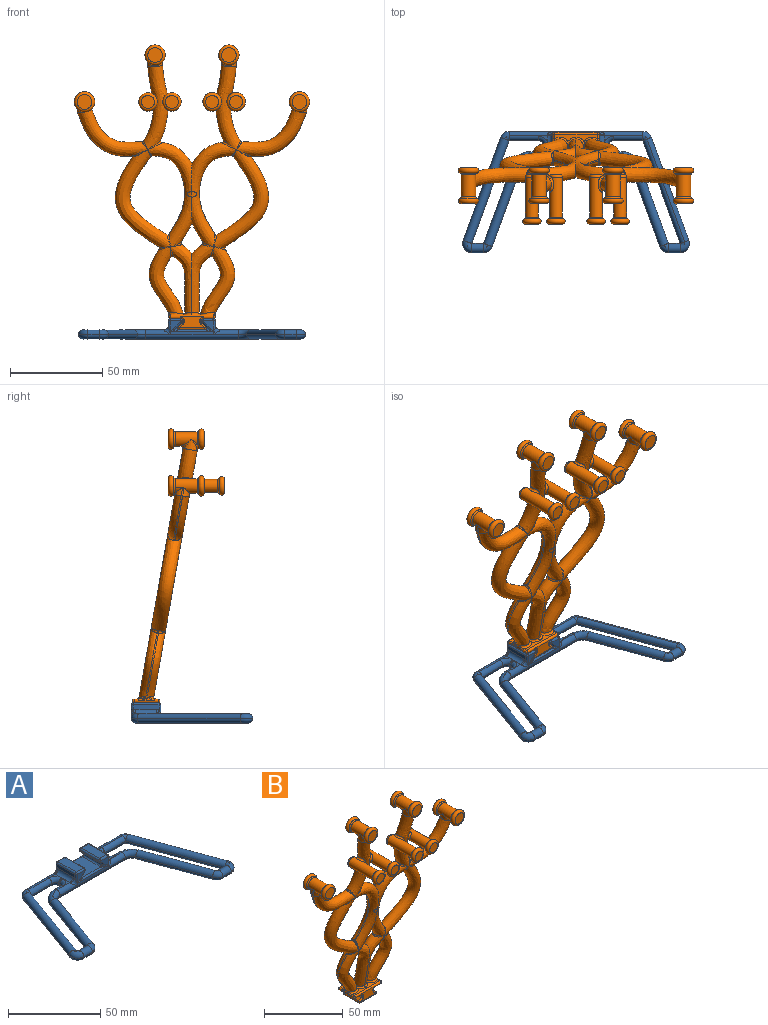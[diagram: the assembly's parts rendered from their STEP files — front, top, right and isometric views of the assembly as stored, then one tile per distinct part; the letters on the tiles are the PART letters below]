
ASSEMBLY  parts=2 mates=1
PART A: 190 faces, bbox 123.8x66.6x10.9 mm
  f0: cylinder r=1mm len=13.55mm, axis (0,1,0), area 31.9mm2, adj f1,f2,f27,f28
  f1: bspline ~1.81x1.19mm, area 1.3mm2, adj f0,f27,f28,f75,f76,f92
  f2: bspline ~1.81x1.19mm, area 1.3mm2, adj f0,f27,f28,f86,f88,f93
  f3: plane 118.01x60.78mm, normal (0,0,-1), area 357mm2, adj f40,f41,f42,f43,f44,f45,f46,f47
  f4: plane 50x7.4mm, normal (0,-1,0), area 70.3mm2, adj f12,f39,f66,f83,f86,f87,f88,f91
  f5: plane 72.41x7.4mm, normal (0,1,0), area 70.3mm2, adj f6,f31,f74,f75,f76,f78,f80,f81
  f6: cylinder r=5mm len=4.7mm, axis (0,0,-1), area 0mm2, adj f5,f7,f32,f73
  f7: plane 55.78x20.3mm, normal (-0.94,0.34,0), area 0mm2, adj f6,f8,f33,f72
  f8: cylinder r=5mm len=6.71mm, axis (0,0,-1), area 0mm2, adj f7,f9,f34,f71
  f9: plane 6.39x0mm, normal (0,-1,0), area 0mm2, adj f8,f10,f35,f70
  f10: cylinder r=5mm len=4.7mm, axis (0,0,-1), area 0mm2, adj f9,f11,f36,f69
  f11: plane 43.2x15.72mm, normal (0.94,-0.34,0), area 0mm2, adj f10,f12,f37,f68
  f12: cylinder r=5mm len=4.7mm, axis (0,0,-1), area 0mm2, adj f4,f11,f38,f67
  f13: plane 60.78x43.76mm, normal (0,0,1), area 10.7mm2, adj f31,f32,f33,f34,f35,f36,f37,f38
  f14: plane 4.75x0mm, normal (0,1,0), area 0mm2, adj f23,f49,f55,f60
  f15: plane 1x0mm, normal (-1,0,0), area 0mm2, adj f50,f51,f55,f56
  f16: plane 15.95x0mm, normal (0,-1,0), area 0mm2, adj f17,f46,f51,f54
  f17: cylinder r=0mm len=0mm, axis (0,0,-1), area 0mm2, adj f16,f18,f44,f57
  f18: plane 55.78x20.3mm, normal (0.94,-0.34,0), area 0mm2, adj f17,f19,f42,f59
  f19: cylinder r=0mm len=0mm, axis (0,0,-1), area 0mm2, adj f18,f20,f40,f61
  f20: plane 6.39x0mm, normal (0,1,0), area 0mm2, adj f19,f21,f41,f63
  f21: cylinder r=0mm len=0mm, axis (0,0,-1), area 0mm2, adj f20,f22,f43,f65
  f22: plane 43.2x15.72mm, normal (-0.94,0.34,0), area 0mm2, adj f21,f23,f45,f64
  f23: cylinder r=10mm len=9.4mm, axis (0,0,-1), area 0mm2, adj f14,f22,f47,f62
  f24: plane 14x2.63mm, normal (-1,0,0), area 33.8mm2, adj f80,f83,f84,f95,f96,f97
  f25: plane 14x0.49mm, normal (1,0,0), area 6.8mm2, adj f29,f30,f78,f91
  f26: plane 14x5.45mm, normal (0,0,1), area 76.3mm2, adj f29,f81,f84,f87
  f27: plane 14.01x13.79mm, normal (0,0,1), area 192.8mm2, adj f0,f1,f2,f75,f86,f99,f100,f101
  f28: plane 14.01x2.01mm, normal (0.71,0,-0.71), area 39.6mm2, adj f0,f1,f2,f30,f76,f88
  f29: cylinder r=1mm len=14mm, axis (0,-1,0), area 22mm2, adj f25,f26,f79,f89
  f30: cylinder r=1mm len=14mm, axis (0,-1,0), area 11mm2, adj f25,f28,f77,f90
  f31: cylinder r=2.5mm len=24.45mm, axis (1,0,0), area 86.4mm2, adj f5,f13,f32,f94,f95
  f32: torus R=2.5mm, axis (0,0,1), area 19.6mm2, adj f6,f13,f31,f33
  f33: cylinder r=2.5mm len=56.63mm, axis (0.34,0.94,0), area 233.1mm2, adj f7,f13,f32,f34
  f34: torus R=2.5mm, axis (0,0,1), area 30.8mm2, adj f8,f13,f33,f35
  f35: cylinder r=2.5mm len=6.39mm, axis (-1,0,0), area 25.1mm2, adj f9,f13,f34,f36
  f36: torus R=2.5mm, axis (0,0,1), area 19.6mm2, adj f10,f13,f35,f37
  f37: cylinder r=2.5mm len=44.05mm, axis (-0.34,-0.94,0), area 180.5mm2, adj f11,f13,f36,f38
  f38: torus R=7.5mm, axis (0,0,1), area 28.3mm2, adj f12,f13,f37,f39
  f39: cylinder r=2.5mm len=13.25mm, axis (-1,0,0), area 42.4mm2, adj f4,f13,f38,f97,f98
  f40: torus R=2.5mm, axis (0,0,1), area 6.8mm2, adj f3,f19,f41,f42
  f41: cylinder r=2.5mm len=6.39mm, axis (-1,0,0), area 25.1mm2, adj f3,f20,f40,f43
  f42: cylinder r=2.5mm len=56.63mm, axis (0.34,0.94,0), area 233.1mm2, adj f3,f18,f40,f44
  f43: torus R=2.5mm, axis (0,0,1), area 4.5mm2, adj f3,f21,f41,f45
  f44: torus R=2.5mm, axis (0,0,1), area 4.4mm2, adj f3,f17,f42,f46
  f45: cylinder r=2.5mm len=44.05mm, axis (-0.34,-0.94,0), area 180.5mm2, adj f3,f22,f43,f47
  f46: cylinder r=2.5mm len=15.95mm, axis (1,0,0), area 62.6mm2, adj f3,f16,f44,f48
  f47: torus R=7.5mm, axis (0,0,1), area 43.6mm2, adj f3,f23,f45,f49
  f48: torus R=5mm, axis (0,0,1), area 21mm2, adj f3,f46,f50,f51
  f49: cylinder r=2.5mm len=4.75mm, axis (-1,0,0), area 18.7mm2, adj f3,f14,f47,f52
  f50: cylinder r=2.5mm len=2.5mm, axis (0,-1,0), area 3.9mm2, adj f3,f15,f48,f52
  f51: cylinder r=2.5mm len=2.5mm, axis (0,0,-1), area 0mm2, adj f15,f16,f48,f53
  f52: torus R=5mm, axis (0,0,1), area 21mm2, adj f3,f49,f50,f55
  f53: torus R=5mm, axis (0,0,1), area 21mm2, adj f13,f51,f54,f56
  f54: cylinder r=2.5mm len=15.95mm, axis (-1,0,0), area 62.6mm2, adj f13,f16,f53,f57
  f55: cylinder r=2.5mm len=2.5mm, axis (0,0,1), area 0mm2, adj f14,f15,f52,f58
  f56: cylinder r=2.5mm len=2.5mm, axis (0,1,0), area 3.9mm2, adj f15,f53,f58,f96
  f57: torus R=2.5mm, axis (0,0,1), area 4.4mm2, adj f13,f17,f54,f59
  f58: torus R=5mm, axis (0,0,1), area 21mm2, adj f13,f55,f56,f60
  f59: cylinder r=2.5mm len=56.63mm, axis (-0.34,-0.94,0), area 233.1mm2, adj f13,f18,f57,f61
  f60: cylinder r=2.5mm len=4.75mm, axis (1,0,0), area 18.7mm2, adj f13,f14,f58,f62
  f61: torus R=2.5mm, axis (0,0,1), area 6.8mm2, adj f13,f19,f59,f63
  f62: torus R=7.5mm, axis (0,0,1), area 43.6mm2, adj f13,f23,f60,f64
  f63: cylinder r=2.5mm len=6.39mm, axis (1,0,0), area 25.1mm2, adj f13,f20,f61,f65
  f64: cylinder r=2.5mm len=44.05mm, axis (0.34,0.94,0), area 180.5mm2, adj f13,f22,f62,f65
  f65: torus R=2.5mm, axis (0,0,1), area 4.5mm2, adj f13,f21,f63,f64
  f66: cylinder r=2.5mm len=50mm, axis (1,0,0), area 196.3mm2, adj f3,f4,f67,f161
  f67: torus R=7.5mm, axis (0,0,1), area 28.3mm2, adj f3,f12,f66,f68
  f68: cylinder r=2.5mm len=44.05mm, axis (0.34,0.94,0), area 180.5mm2, adj f3,f11,f67,f69
  f69: torus R=2.5mm, axis (0,0,1), area 19.6mm2, adj f3,f10,f68,f70
  f70: cylinder r=2.5mm len=6.39mm, axis (1,0,0), area 25.1mm2, adj f3,f9,f69,f71
  f71: torus R=2.5mm, axis (0,0,1), area 30.8mm2, adj f3,f8,f70,f72
  f72: cylinder r=2.5mm len=56.63mm, axis (-0.34,-0.94,0), area 233.1mm2, adj f3,f7,f71,f73
  f73: torus R=2.5mm, axis (0,0,1), area 19.6mm2, adj f3,f6,f72,f74
  f74: cylinder r=2.5mm len=72.41mm, axis (-1,0,0), area 284.3mm2, adj f3,f5,f73,f167
  f75: cylinder r=1mm len=23.43mm, axis (1,0,0), area 27.2mm2, adj f1,f5,f27,f92,f100,f183
  f76: cylinder r=1mm len=6.12mm, axis (-0.71,0,-0.71), area 7.2mm2, adj f1,f5,f28,f77,f92
  f77: sphere r=1mm, area 0.6mm2, adj f30,f76,f78
  f78: cylinder r=1mm len=1mm, axis (0,0,1), area 0.8mm2, adj f5,f25,f77,f79
  f79: sphere r=1mm, area 1mm2, adj f29,f78,f81
  f80: cylinder r=1mm len=7.4mm, axis (0,0,-1), area 7.9mm2, adj f5,f24,f82,f94
  f81: cylinder r=1mm len=5.45mm, axis (1,0,0), area 8.6mm2, adj f5,f26,f79,f82
  f82: sphere r=1mm, area 2.1mm2, adj f80,f81,f84
  f83: cylinder r=1mm len=7.4mm, axis (0,0,1), area 7.9mm2, adj f4,f24,f85,f98
  f84: cylinder r=1mm len=14mm, axis (0,1,0), area 22mm2, adj f24,f26,f82,f85
  f85: sphere r=1mm, area 1.6mm2, adj f83,f84,f87
  f86: cylinder r=1mm len=23.43mm, axis (-1,0,0), area 27.2mm2, adj f2,f4,f27,f93,f101,f184
  f87: cylinder r=1mm len=5.45mm, axis (-1,0,0), area 8.6mm2, adj f4,f26,f85,f89
  f88: cylinder r=1mm len=6.12mm, axis (0.71,0,0.71), area 7.2mm2, adj f2,f4,f28,f90,f93
  f89: sphere r=1mm, area 1.6mm2, adj f29,f87,f91
  f90: sphere r=1mm, area 0.8mm2, adj f30,f88,f91
  f91: cylinder r=1mm len=1mm, axis (0,0,-1), area 0.8mm2, adj f4,f25,f89,f90
  f92: bspline ~4.44x2.49mm, area 2.3mm2, adj f1,f75,f76
  f93: bspline ~4.31x2.42mm, area 2.3mm2, adj f2,f86,f88
  f94: bspline ~4.82x3.5mm, area 4.6mm2, adj f31,f80,f95
  f95: torus R=5mm, axis (-1,0,0), area 4.1mm2, adj f24,f31,f94,f96
  f96: cylinder r=2.5mm len=11mm, axis (0,-1,0), area 43.2mm2, adj f13,f24,f56,f95,f97
  f97: torus R=5mm, axis (-1,0,0), area 4.1mm2, adj f24,f39,f96,f98
  f98: bspline ~4.82x3.5mm, area 4.6mm2, adj f39,f83,f97
  f99: cylinder r=1mm len=13.55mm, axis (0,1,0), area 31.9mm2, adj f27,f100,f101,f123
  f100: bspline ~1.81x1.2mm, area 1.3mm2, adj f27,f75,f99,f123,f168,f183
  f101: bspline ~1.81x1.2mm, area 1.3mm2, adj f27,f86,f99,f123,f179,f184
  f102: cylinder r=5mm len=4.7mm, axis (0,0,-1), area 0mm2, adj f5,f103,f127,f167
  f103: plane 55.78x20.3mm, normal (0.94,0.34,0), area 0mm2, adj f102,f104,f128,f166
  f104: cylinder r=5mm len=6.71mm, axis (0,0,-1), area 0mm2, adj f103,f105,f129,f165
  f105: plane 6.39x0mm, normal (0,-1,0), area 0mm2, adj f104,f106,f130,f164
  f106: cylinder r=5mm len=4.7mm, axis (0,0,-1), area 0mm2, adj f105,f107,f131,f163
  f107: plane 43.2x15.72mm, normal (-0.94,-0.34,0), area 0mm2, adj f106,f108,f132,f162
  f108: cylinder r=5mm len=4.7mm, axis (0,0,-1), area 0mm2, adj f4,f107,f133,f161
  f109: plane 60.78x43.76mm, normal (0,0,1), area 10.7mm2, adj f126,f127,f128,f129,f130,f131,f132,f133
  f110: plane 4.75x0mm, normal (0,1,0), area 0mm2, adj f119,f144,f150,f155
  f111: plane 1x0mm, normal (1,0,0), area 0mm2, adj f145,f146,f150,f151
  f112: plane 15.95x0mm, normal (0,-1,0), area 0mm2, adj f113,f141,f146,f149
  f113: cylinder r=0mm len=0mm, axis (0,0,-1), area 0mm2, adj f112,f114,f139,f152
  f114: plane 55.78x20.3mm, normal (-0.94,-0.34,0), area 0mm2, adj f113,f115,f137,f154
  f115: cylinder r=0mm len=0mm, axis (0,0,-1), area 0mm2, adj f114,f116,f135,f156
  f116: plane 6.39x0mm, normal (0,1,0), area 0mm2, adj f115,f117,f136,f158
  f117: cylinder r=0mm len=0mm, axis (0,0,-1), area 0mm2, adj f116,f118,f138,f160
  f118: plane 43.2x15.72mm, normal (0.94,0.34,0), area 0mm2, adj f117,f119,f140,f159
  f119: cylinder r=10mm len=9.4mm, axis (0,0,-1), area 0mm2, adj f110,f118,f142,f157
  f120: plane 14x2.63mm, normal (1,0,0), area 33.8mm2, adj f172,f175,f176,f186,f187,f188
  f121: plane 14x0.49mm, normal (-1,0,0), area 6.8mm2, adj f124,f125,f170,f182
  f122: plane 14x5.45mm, normal (0,0,1), area 76.3mm2, adj f124,f173,f176,f178
  f123: plane 14.01x2.01mm, normal (-0.71,0,-0.71), area 39.6mm2, adj f99,f100,f101,f125,f168,f179
  f124: cylinder r=1mm len=14mm, axis (0,-1,0), area 22mm2, adj f121,f122,f171,f180
  f125: cylinder r=1mm len=14mm, axis (0,-1,0), area 11mm2, adj f121,f123,f169,f181
  f126: cylinder r=2.5mm len=24.45mm, axis (-1,0,0), area 86.4mm2, adj f5,f109,f127,f185,f186
  f127: torus R=2.5mm, axis (0,0,1), area 19.6mm2, adj f102,f109,f126,f128
  f128: cylinder r=2.5mm len=56.63mm, axis (-0.34,0.94,0), area 233.1mm2, adj f103,f109,f127,f129
  f129: torus R=2.5mm, axis (0,0,1), area 30.8mm2, adj f104,f109,f128,f130
  f130: cylinder r=2.5mm len=6.39mm, axis (1,0,0), area 25.1mm2, adj f105,f109,f129,f131
  f131: torus R=2.5mm, axis (0,0,1), area 19.6mm2, adj f106,f109,f130,f132
  f132: cylinder r=2.5mm len=44.05mm, axis (0.34,-0.94,0), area 180.5mm2, adj f107,f109,f131,f133
  f133: torus R=7.5mm, axis (0,0,1), area 28.3mm2, adj f108,f109,f132,f134
  f134: cylinder r=2.5mm len=13.25mm, axis (1,0,0), area 42.4mm2, adj f4,f109,f133,f188,f189
  f135: torus R=2.5mm, axis (0,0,1), area 6.8mm2, adj f3,f115,f136,f137
  f136: cylinder r=2.5mm len=6.39mm, axis (1,0,0), area 25.1mm2, adj f3,f116,f135,f138
  f137: cylinder r=2.5mm len=56.63mm, axis (-0.34,0.94,0), area 233.1mm2, adj f3,f114,f135,f139
  f138: torus R=2.5mm, axis (0,0,1), area 4.5mm2, adj f3,f117,f136,f140
  f139: torus R=2.5mm, axis (0,0,1), area 4.4mm2, adj f3,f113,f137,f141
  f140: cylinder r=2.5mm len=44.05mm, axis (0.34,-0.94,0), area 180.5mm2, adj f3,f118,f138,f142
  f141: cylinder r=2.5mm len=15.95mm, axis (-1,0,0), area 62.6mm2, adj f3,f112,f139,f143
  f142: torus R=7.5mm, axis (0,0,1), area 43.6mm2, adj f3,f119,f140,f144
  f143: torus R=5mm, axis (0,0,1), area 21mm2, adj f3,f141,f145,f146
  f144: cylinder r=2.5mm len=4.75mm, axis (1,0,0), area 18.7mm2, adj f3,f110,f142,f147
  f145: cylinder r=2.5mm len=2.5mm, axis (0,-1,0), area 3.9mm2, adj f3,f111,f143,f147
  f146: cylinder r=2.5mm len=2.5mm, axis (0,0,-1), area 0mm2, adj f111,f112,f143,f148
  f147: torus R=5mm, axis (0,0,1), area 21mm2, adj f3,f144,f145,f150
  f148: torus R=5mm, axis (0,0,1), area 21mm2, adj f109,f146,f149,f151
  f149: cylinder r=2.5mm len=15.95mm, axis (1,0,0), area 62.6mm2, adj f109,f112,f148,f152
  f150: cylinder r=2.5mm len=2.5mm, axis (0,0,1), area 0mm2, adj f110,f111,f147,f153
  f151: cylinder r=2.5mm len=2.5mm, axis (0,1,0), area 3.9mm2, adj f111,f148,f153,f187
  f152: torus R=2.5mm, axis (0,0,1), area 4.4mm2, adj f109,f113,f149,f154
  f153: torus R=5mm, axis (0,0,1), area 21mm2, adj f109,f150,f151,f155
  f154: cylinder r=2.5mm len=56.63mm, axis (0.34,-0.94,0), area 233.1mm2, adj f109,f114,f152,f156
  f155: cylinder r=2.5mm len=4.75mm, axis (-1,0,0), area 18.7mm2, adj f109,f110,f153,f157
  f156: torus R=2.5mm, axis (0,0,1), area 6.8mm2, adj f109,f115,f154,f158
  f157: torus R=7.5mm, axis (0,0,1), area 43.6mm2, adj f109,f119,f155,f159
  f158: cylinder r=2.5mm len=6.39mm, axis (-1,0,0), area 25.1mm2, adj f109,f116,f156,f160
  f159: cylinder r=2.5mm len=44.05mm, axis (-0.34,0.94,0), area 180.5mm2, adj f109,f118,f157,f160
  f160: torus R=2.5mm, axis (0,0,1), area 4.5mm2, adj f109,f117,f158,f159
  f161: torus R=7.5mm, axis (0,0,1), area 28.3mm2, adj f3,f66,f108,f162
  f162: cylinder r=2.5mm len=44.05mm, axis (-0.34,0.94,0), area 180.5mm2, adj f3,f107,f161,f163
  f163: torus R=2.5mm, axis (0,0,1), area 19.6mm2, adj f3,f106,f162,f164
  f164: cylinder r=2.5mm len=6.39mm, axis (-1,0,0), area 25.1mm2, adj f3,f105,f163,f165
  f165: torus R=2.5mm, axis (0,0,1), area 30.8mm2, adj f3,f104,f164,f166
  f166: cylinder r=2.5mm len=56.63mm, axis (0.34,-0.94,0), area 233.1mm2, adj f3,f103,f165,f167
  f167: torus R=2.5mm, axis (0,0,1), area 19.6mm2, adj f3,f74,f102,f166
  f168: cylinder r=1mm len=6.12mm, axis (0.71,0,-0.71), area 7.2mm2, adj f5,f100,f123,f169,f183
  f169: sphere r=1mm, area 0.6mm2, adj f125,f168,f170
  f170: cylinder r=1mm len=1mm, axis (0,0,1), area 0.8mm2, adj f5,f121,f169,f171
  f171: sphere r=1mm, area 2.1mm2, adj f124,f170,f173
  f172: cylinder r=1mm len=7.4mm, axis (0,0,-1), area 7.9mm2, adj f5,f120,f174,f185
  f173: cylinder r=1mm len=5.45mm, axis (-1,0,0), area 8.6mm2, adj f5,f122,f171,f174
  f174: sphere r=1mm, area 1.6mm2, adj f172,f173,f176
  f175: cylinder r=1mm len=7.4mm, axis (0,0,1), area 7.9mm2, adj f4,f120,f177,f189
  f176: cylinder r=1mm len=14mm, axis (0,1,0), area 22mm2, adj f120,f122,f174,f177
  f177: sphere r=1mm, area 2.1mm2, adj f175,f176,f178
  f178: cylinder r=1mm len=5.45mm, axis (1,0,0), area 8.6mm2, adj f4,f122,f177,f180
  f179: cylinder r=1mm len=6.12mm, axis (-0.71,0,0.71), area 7.2mm2, adj f4,f101,f123,f181,f184
  f180: sphere r=1mm, area 1.6mm2, adj f124,f178,f182
  f181: sphere r=1mm, area 0.6mm2, adj f125,f179,f182
  f182: cylinder r=1mm len=1mm, axis (0,0,-1), area 0.8mm2, adj f4,f121,f180,f181
  f183: bspline ~4.44x2.49mm, area 2.3mm2, adj f75,f100,f168
  f184: bspline ~4.31x2.42mm, area 2.3mm2, adj f86,f101,f179
  f185: bspline ~4.93x3.5mm, area 4.6mm2, adj f126,f172,f186
  f186: torus R=5mm, axis (1,0,0), area 4.1mm2, adj f120,f126,f185,f187
  f187: cylinder r=2.5mm len=11mm, axis (0,-1,0), area 43.2mm2, adj f109,f120,f151,f186,f188
  f188: torus R=5mm, axis (1,0,0), area 4.1mm2, adj f120,f134,f187,f189
  f189: bspline ~4.93x3.5mm, area 4.6mm2, adj f134,f175,f188
PART B: 206 faces, bbox 128.4x50.5x154.9 mm
  f0: bspline ~3.73x3.2mm, area 1.2mm2, adj f1,f201,f202
  f1: bspline ~8.82x7.96mm, area 52.9mm2, adj f0,f2,f8,f9,f200
  f2: bspline ~3.64x3.12mm, area 1.2mm2, adj f1,f3,f7
  f3: cylinder r=4mm len=2.76mm, axis (0,1,0), area 4mm2, adj f2,f4,f202
  f4: torus R=5mm, axis (0,1,0), area 22.5mm2, adj f3,f5,f7,f201,f202
  f5: torus R=4mm, axis (0,-1,0), area 125.8mm2, adj f4,f6,f8
  f6: plane 8x8mm, normal (0,-1,0), area 50.3mm2, adj f5
  f7: sphere r=1mm, area 0.4mm2, adj f2,f4,f8
  f8: bspline ~7.57x4.15mm, area 15.5mm2, adj f1,f5,f7,f201
  f9: bspline ~48.84x16.11mm, area 975.3mm2, adj f1,f10,f17,f18,f25,f26,f199,f200
  f10: bspline ~7.55x3.25mm, area 11.5mm2, adj f9,f11,f17
  f11: torus R=2mm, axis (0,-1,0), area 39.2mm2, adj f10,f12,f13
  f12: plane 4x4mm, normal (0,1,0), area 12.6mm2, adj f11
  f13: cylinder r=3.5mm len=21.61mm, axis (0,1,0), area 413.1mm2, adj f11,f14,f17
  f14: torus R=4.5mm, axis (0,1,0), area 27mm2, adj f13,f15
  f15: torus R=3.5mm, axis (0,-1,0), area 117.2mm2, adj f14,f16
  f16: plane 7x7mm, normal (0,-1,0), area 38.5mm2, adj f15
  f17: bspline ~8.42x8.17mm, area 36.7mm2, adj f9,f10,f13
  f18: bspline ~6.7x2.93mm, area 11.2mm2, adj f9,f19,f25
  f19: torus R=2mm, axis (0,-1,0), area 41.2mm2, adj f18,f20,f21
  f20: plane 4x4mm, normal (0,1,0), area 12.6mm2, adj f19
  f21: cylinder r=3.5mm len=21.61mm, axis (0,1,0), area 420.2mm2, adj f19,f22,f25
  f22: torus R=4.5mm, axis (0,1,0), area 27mm2, adj f21,f23
  f23: torus R=3.5mm, axis (0,-1,0), area 117.2mm2, adj f22,f24
  f24: plane 7x7mm, normal (0,-1,0), area 38.5mm2, adj f23
  f25: bspline ~8.73x7.85mm, area 40.8mm2, adj f9,f18,f21
  f26: bspline ~7.88x4.85mm, area 0mm2, adj f9,f27
  f27: bspline ~50.27x27.35mm, area 990.1mm2, adj f26,f28,f195,f196,f197,f198
  f28: bspline ~32.42x24.8mm, area 4.8mm2, adj f27,f29,f183,f194,f198
  f29: bspline ~39.8x25.9mm, area 31.2mm2, adj f28,f30,f31,f183,f194,f197
  f30: bspline ~6.71x4.07mm, area 2.7mm2, adj f29,f31,f196,f197
  f31: bspline ~58.65x32.66mm, area 1554.9mm2, adj f29,f30,f32,f175,f176,f177,f178,f179
  f32: bspline ~2.21x1.05mm, area 0.8mm2, adj f31,f33,f175,f180,f182
  f33: bspline ~59.64x28.84mm, area 822.2mm2, adj f32,f34,f36,f174,f175,f179,f180,f181
  f34: bspline ~27.94x12.28mm, area 6.3mm2, adj f33,f35
  f35: bspline ~27.94x12.28mm, area 6.3mm2, adj f34,f36
  f36: bspline ~69.76x34.56mm, area 1244mm2, adj f33,f35,f37,f168,f169,f170,f171,f172
  f37: bspline ~4.79x3mm, area 2.2mm2, adj f36,f38,f171
  f38: bspline ~58.65x32.66mm, area 1556.8mm2, adj f37,f39,f87,f88,f89,f90,f166,f167
  f39: bspline ~9.5x6.18mm, area 4.2mm2, adj f38,f40,f87
  f40: bspline ~50.27x27.35mm, area 993mm2, adj f39,f41,f73,f86,f87,f89
  f41: bspline ~7.88x4.85mm, area 0mm2, adj f40,f42
  f42: bspline ~48.84x16.11mm, area 975.4mm2, adj f41,f43,f50,f51,f58,f59,f72,f173
  f43: bspline ~6.7x2.93mm, area 11.2mm2, adj f42,f44,f50
  f44: torus R=2mm, axis (0,-1,0), area 41.2mm2, adj f43,f45,f49
  f45: cylinder r=3.5mm len=21.61mm, axis (0,1,0), area 420.2mm2, adj f44,f46,f50
  f46: torus R=4.5mm, axis (0,-1,0), area 27mm2, adj f45,f47
  f47: torus R=3.5mm, axis (0,-1,0), area 117.2mm2, adj f46,f48
  f48: plane 7x7mm, normal (0,-1,0), area 38.5mm2, adj f47
  f49: plane 4x4mm, normal (0,1,0), area 12.6mm2, adj f44
  f50: bspline ~8.73x7.85mm, area 40.8mm2, adj f42,f43,f45
  f51: bspline ~7.55x3.25mm, area 11.5mm2, adj f42,f52,f58
  f52: torus R=2mm, axis (0,-1,0), area 39.2mm2, adj f51,f53,f57
  f53: cylinder r=3.5mm len=21.61mm, axis (0,1,0), area 413.1mm2, adj f52,f54,f58
  f54: torus R=4.5mm, axis (0,-1,0), area 27mm2, adj f53,f55
  f55: torus R=3.5mm, axis (0,-1,0), area 117.2mm2, adj f54,f56
  f56: plane 7x7mm, normal (0,-1,0), area 38.5mm2, adj f55
  f57: plane 4x4mm, normal (0,1,0), area 12.6mm2, adj f52
  f58: bspline ~8.42x8.17mm, area 36.7mm2, adj f42,f51,f53
  f59: bspline ~8x5.9mm, area 3.3mm2, adj f42,f60,f72
  f60: cylinder r=4mm len=11.82mm, axis (0,1,0), area 223.2mm2, adj f59,f61,f67,f68,f69
  f61: bspline ~3.64x3.12mm, area 1.2mm2, adj f60,f62,f72
  f62: sphere r=1mm, area 0.4mm2, adj f61,f63,f68
  f63: bspline ~7.57x4.15mm, area 15.5mm2, adj f62,f64,f65,f72
  f64: sphere r=1mm, area 0.4mm2, adj f63,f67,f68
  f65: torus R=4mm, axis (0,-1,0), area 125.8mm2, adj f63,f66,f68
  f66: plane 8x8mm, normal (0,-1,0), area 50.3mm2, adj f65
  f67: bspline ~3.73x3.2mm, area 1.2mm2, adj f60,f64,f72
  f68: torus R=5mm, axis (0,-1,0), area 22.5mm2, adj f60,f62,f64,f65
  f69: torus R=5mm, axis (0,1,0), area 30.7mm2, adj f60,f70
  f70: torus R=4mm, axis (0,1,0), area 130mm2, adj f69,f71
  f71: plane 8x8mm, normal (0,1,0), area 50.3mm2, adj f70
  f72: bspline ~8.82x7.96mm, area 52.9mm2, adj f42,f59,f61,f63,f67
  f73: bspline ~36.61x24.53mm, area 4.7mm2, adj f40,f74,f86,f87,f88
  f74: plane 4.36x1.53mm, normal (-1,-0.04,0.01), area 3.4mm2, adj f73,f75,f86,f87
  f75: bspline ~0.82x0.36mm, area 0.1mm2, adj f74,f76,f77,f86
  f76: bspline ~10.31x9.4mm, area 0mm2, adj f75,f77,f86
  f77: cylinder r=4mm len=11.82mm, axis (0,1,0), area 229.2mm2, adj f75,f76,f78,f79,f80,f83,f86
  f78: bspline ~16.75x10.3mm, area 0mm2, adj f77
  f79: cylinder r=4mm len=4.35mm, axis (0,1,0), area 9.3mm2, adj f77,f80,f86
  f80: torus R=5mm, axis (0,1,0), area 30.5mm2, adj f77,f79,f81,f86
  f81: torus R=4mm, axis (0,1,0), area 130mm2, adj f80,f82
  f82: plane 8x8mm, normal (0,1,0), area 50.3mm2, adj f81
  f83: torus R=5mm, axis (0,-1,0), area 30.7mm2, adj f77,f84
  f84: torus R=4mm, axis (0,-1,0), area 130mm2, adj f83,f85
  f85: plane 8x8mm, normal (0,-1,0), area 50.3mm2, adj f84
  f86: bspline ~16.75x10.31mm, area 50.5mm2, adj f40,f73,f74,f75,f76,f77,f79,f80
  f87: bspline ~39.78x25.84mm, area 34mm2, adj f38,f39,f40,f73,f74,f88
  f88: bspline ~6.71x4.07mm, area 2.7mm2, adj f38,f73,f87,f89
  f89: bspline ~9.64x5.17mm, area 5.6mm2, adj f38,f40,f88
  f90: bspline ~6.45x4.37mm, area 6.4mm2, adj f38,f91,f166
  f91: bspline ~54.44x24.59mm, area 927.5mm2, adj f90,f92,f160,f161,f162,f163,f164,f165
  f92: bspline ~2.09x1.72mm, area 0.9mm2, adj f91,f93,f94,f160,f164
  f93: bspline ~0.63x0.31mm, area 0.1mm2, adj f92,f94,f162,f163
  f94: bspline ~0.72x0.68mm, area 0mm2, adj f92,f93,f95
  f95: bspline ~2.63x1.63mm, area 2.7mm2, adj f94,f96,f160,f162
  f96: cylinder r=1mm len=13mm, axis (0,-1,0), area 27.5mm2, adj f95,f97,f156,f157,f158,f159,f161,f162
  f97: plane 23.05x3.9mm, normal (0,0,1), area 44.7mm2, adj f96,f98,f113,f114,f115,f155,f160
  f98: bspline ~10.03x6.12mm, area 19.3mm2, adj f97,f99,f113,f159,f160
  f99: bspline ~40.69x18.8mm, area 595.8mm2, adj f98,f100,f101,f102,f165,f169
  f100: bspline ~20.54x11.62mm, area 0mm2, adj f99,f102
  f101: bspline ~20.54x11.62mm, area 0mm2, adj f99,f102
  f102: bspline ~40.69x18.8mm, area 595.8mm2, adj f99,f100,f101,f103,f113,f174
  f103: bspline ~7.89x7.19mm, area 0mm2, adj f102,f104
  f104: bspline ~54.44x24.59mm, area 927.5mm2, adj f103,f105,f106,f110,f111,f112,f114,f176
  f105: bspline ~43.42x13.65mm, area 32.4mm2, adj f104,f106,f112,f177
  f106: bspline ~2.18x1.77mm, area 0.9mm2, adj f104,f105,f107,f109,f114
  f107: bspline ~0.64x0.6mm, area 0mm2, adj f106,f108,f109
  f108: bspline ~2.63x1.63mm, area 2.7mm2, adj f107,f111,f114,f115
  f109: bspline ~0.78x0.37mm, area 0.1mm2, adj f106,f107,f111,f112
  f110: bspline ~2.91x2.83mm, area 3.3mm2, adj f104,f111,f114,f115
  f111: plane 8.48x1.95mm, normal (1,0,0), area 5.8mm2, adj f104,f108,f109,f110,f112,f115
  f112: bspline ~2.59x0.28mm, area 0.4mm2, adj f104,f105,f109,f111
  f113: bspline ~10.03x6.12mm, area 19.3mm2, adj f97,f98,f102,f114,f159
  f114: bspline ~10.19x10.05mm, area 32.5mm2, adj f97,f104,f106,f108,f110,f113,f159
  f115: cylinder r=1mm len=13mm, axis (0,-1,0), area 27.5mm2, adj f97,f108,f110,f111,f116,f153,f154,f159
  f116: sphere r=1mm, area 3.1mm2, adj f115,f117
  f117: cylinder r=1mm len=23.04mm, axis (1,0,0), area 52.7mm2, adj f116,f118,f151,f152,f153,f157,f158,f159
  f118: torus R=2mm, axis (0,-1,0), area 3.4mm2, adj f117,f119,f150,f151
  f119: cylinder r=1mm len=13mm, axis (0,1,0), area 20.4mm2, adj f118,f120,f149,f157
  f120: plane 13x0.65mm, normal (-1,0,0), area 8.4mm2, adj f119,f121,f148,f150
  f121: cylinder r=1mm len=1mm, axis (0,0,1), area 1mm2, adj f120,f122,f147,f149
  f122: plane 13.57x6mm, normal (0,-1,0), area 59.4mm2, adj f121,f123,f142,f143,f144,f145,f146,f147
  f123: cylinder r=1mm len=2.65mm, axis (-0.71,0,0.71), area 4.3mm2, adj f122,f124,f141,f146
  f124: plane 13x1.94mm, normal (0.71,0,0.71), area 35.6mm2, adj f123,f125,f135,f140
  f125: cylinder r=1mm len=13mm, axis (0,1,0), area 30.6mm2, adj f124,f126,f134,f141
  f126: plane 13.57x13mm, normal (0,0,-1), area 176.4mm2, adj f125,f127,f132,f142
  f127: cylinder r=1mm len=13.57mm, axis (1,0,0), area 21.3mm2, adj f126,f128,f134,f151
  f128: sphere r=1mm, area 2.2mm2, adj f127,f129,f132
  f129: cylinder r=1mm len=2.65mm, axis (-0.71,0,-0.71), area 4.3mm2, adj f128,f130,f131,f151
  f130: plane 13x1.94mm, normal (-0.71,0,0.71), area 35.6mm2, adj f129,f132,f143,f148
  f131: torus R=2mm, axis (0,-1,0), area 1.7mm2, adj f129,f148,f150,f151
  f132: cylinder r=1mm len=13mm, axis (0,1,0), area 30.6mm2, adj f126,f128,f130,f133
  f133: sphere r=1mm, area 2.2mm2, adj f132,f142,f143
  f134: sphere r=1mm, area 2.2mm2, adj f125,f127,f140
  f135: cylinder r=1mm len=13mm, axis (0,-1,0), area 10.2mm2, adj f124,f136,f138,f146
  f136: torus R=2mm, axis (0,-1,0), area 1.7mm2, adj f135,f137,f140,f151
  f137: cylinder r=1mm len=1mm, axis (0,0,-1), area 1mm2, adj f136,f138,f151,f152
  f138: plane 13x0.65mm, normal (1,0,0), area 8.4mm2, adj f135,f137,f139,f145
  f139: cylinder r=1mm len=13mm, axis (0,1,0), area 20.4mm2, adj f138,f144,f152,f153
  f140: cylinder r=1mm len=2.65mm, axis (0.71,0,-0.71), area 4.3mm2, adj f124,f134,f136,f151
  f141: sphere r=1mm, area 2.4mm2, adj f123,f125,f142
  f142: cylinder r=1mm len=13.57mm, axis (-1,0,0), area 21.3mm2, adj f122,f126,f133,f141
  f143: cylinder r=1mm len=2.65mm, axis (0.71,0,0.71), area 4.3mm2, adj f122,f130,f133,f147
  f144: torus R=2mm, axis (0,-1,0), area 3.4mm2, adj f122,f139,f145,f155
  f145: cylinder r=1mm len=1mm, axis (0,0,1), area 1mm2, adj f122,f138,f144,f146
  f146: torus R=2mm, axis (0,-1,0), area 1.7mm2, adj f122,f123,f135,f145
  f147: torus R=2mm, axis (0,-1,0), area 1.7mm2, adj f121,f122,f143,f148
  f148: cylinder r=1mm len=13mm, axis (0,-1,0), area 10.2mm2, adj f120,f130,f131,f147
  f149: torus R=2mm, axis (0,-1,0), area 3.4mm2, adj f119,f121,f122,f155
  f150: cylinder r=1mm len=1mm, axis (0,0,-1), area 1mm2, adj f118,f120,f131,f151
  f151: plane 13.57x6mm, normal (0,1,0), area 59.4mm2, adj f117,f118,f127,f129,f131,f136,f137,f140
  f152: torus R=2mm, axis (0,-1,0), area 3.4mm2, adj f117,f137,f139,f151
  f153: plane 13x5.26mm, normal (0,0,-1), area 68.4mm2, adj f115,f117,f139,f155
  f154: sphere r=1mm, area 3.1mm2, adj f115,f155
  f155: cylinder r=1mm len=23.04mm, axis (-1,0,0), area 52.7mm2, adj f97,f122,f144,f149,f153,f154,f156,f157
  f156: sphere r=1mm, area 3.1mm2, adj f96,f155
  f157: plane 13x5.26mm, normal (0,0,-1), area 68.4mm2, adj f96,f117,f119,f155
  f158: sphere r=1mm, area 4.7mm2, adj f96,f117
  f159: plane 23.05x4.2mm, normal (0,0,1), area 52.5mm2, adj f96,f98,f113,f114,f115,f117,f160
  f160: bspline ~10.21x10.05mm, area 32.6mm2, adj f91,f92,f95,f97,f98,f159,f161
  f161: bspline ~2.91x2.83mm, area 3.3mm2, adj f91,f96,f160,f162
  f162: plane 8.48x1.95mm, normal (-1,0,0), area 5.8mm2, adj f91,f93,f95,f96,f161,f163
  f163: bspline ~2.59x0.28mm, area 0.4mm2, adj f91,f93,f162,f164
  f164: bspline ~43.42x13.25mm, area 32.4mm2, adj f91,f92,f163,f166
  f165: bspline ~7.89x7.19mm, area 0mm2, adj f91,f99
  f166: bspline ~1.82x1.62mm, area 1.1mm2, adj f38,f90,f91,f164,f167
  f167: bspline ~6.2x3.61mm, area 4.1mm2, adj f38,f91,f166
  f168: bspline ~5.51x4.87mm, area 2.4mm2, adj f36,f38,f171
  f169: bspline ~7.76x6.34mm, area 0mm2, adj f36,f99
  f170: bspline ~6.91x2.89mm, area 3.1mm2, adj f36,f38,f171
  f171: bspline ~49.57x25.73mm, area 50.8mm2, adj f36,f37,f38,f168,f170,f172
  f172: bspline ~4.51x3.79mm, area 1.7mm2, adj f36,f38,f171
  f173: bspline ~8.17x7.92mm, area 0mm2, adj f36,f42
  f174: bspline ~7.76x6.34mm, area 0mm2, adj f33,f102
  f175: bspline ~4.79x3mm, area 2.4mm2, adj f31,f32,f33
  f176: bspline ~6.45x4.37mm, area 6.4mm2, adj f31,f104,f177
  f177: bspline ~1.82x1.62mm, area 1.1mm2, adj f31,f104,f105,f176,f178
  f178: bspline ~6.2x3.61mm, area 4.1mm2, adj f31,f104,f177
  f179: bspline ~5.51x4.87mm, area 3.6mm2, adj f31,f33,f180
  f180: bspline ~49.59x25.82mm, area 44.3mm2, adj f31,f32,f33,f179,f181
  f181: bspline ~6.91x2.89mm, area 3.1mm2, adj f31,f33,f180
  f182: bspline ~5.33x3.79mm, area 2.4mm2, adj f31,f32,f33
  f183: plane 4.36x1.53mm, normal (1,-0.04,0.01), area 3.4mm2, adj f28,f29,f184,f197,f198
  f184: bspline ~0.82x0.36mm, area 0.1mm2, adj f183,f185,f186,f198
  f185: bspline ~10.31x9.4mm, area 0mm2, adj f184,f186,f198
  f186: cylinder r=4mm len=11.82mm, axis (0,1,0), area 236.5mm2, adj f184,f185,f187,f188,f191,f198
  f187: bspline ~16.75x10.3mm, area 0mm2, adj f186
  f188: torus R=5mm, axis (0,-1,0), area 30.5mm2, adj f186,f189,f198
  f189: torus R=4mm, axis (0,1,0), area 130mm2, adj f188,f190
  f190: plane 8x8mm, normal (0,1,0), area 50.3mm2, adj f189
  f191: torus R=5mm, axis (0,1,0), area 30.7mm2, adj f186,f192
  f192: torus R=4mm, axis (0,-1,0), area 130mm2, adj f191,f193
  f193: plane 8x8mm, normal (0,-1,0), area 50.3mm2, adj f192
  f194: bspline ~6.32x3.76mm, area 2.7mm2, adj f28,f29,f31,f195
  f195: bspline ~9.49x6.16mm, area 5.6mm2, adj f27,f31,f194
  f196: bspline ~9.64x5.17mm, area 5.6mm2, adj f27,f30,f31
  f197: bspline ~36.61x24.53mm, area 4.7mm2, adj f27,f29,f30,f183,f198
  f198: bspline ~16.75x10.31mm, area 50.5mm2, adj f27,f28,f183,f184,f185,f186,f188,f197
  f199: bspline ~8.17x7.92mm, area 0mm2, adj f9,f33
  f200: bspline ~8x5.9mm, area 9.8mm2, adj f1,f9,f202
  f201: sphere r=1mm, area 0.4mm2, adj f0,f4,f8
  f202: cylinder r=4mm len=11.82mm, axis (0,1,0), area 219.2mm2, adj f0,f3,f4,f200,f203
  f203: torus R=5mm, axis (0,-1,0), area 30.7mm2, adj f202,f204
  f204: torus R=4mm, axis (0,1,0), area 130mm2, adj f203,f205
  f205: plane 8x8mm, normal (0,1,0), area 50.3mm2, adj f204
PLACE A at identity fixed
PLACE B t=(0,35.5,5)mm
MATE fastened B.f126 <-> A.f27  axis (0,0,-1) through (0,28,5)mm
